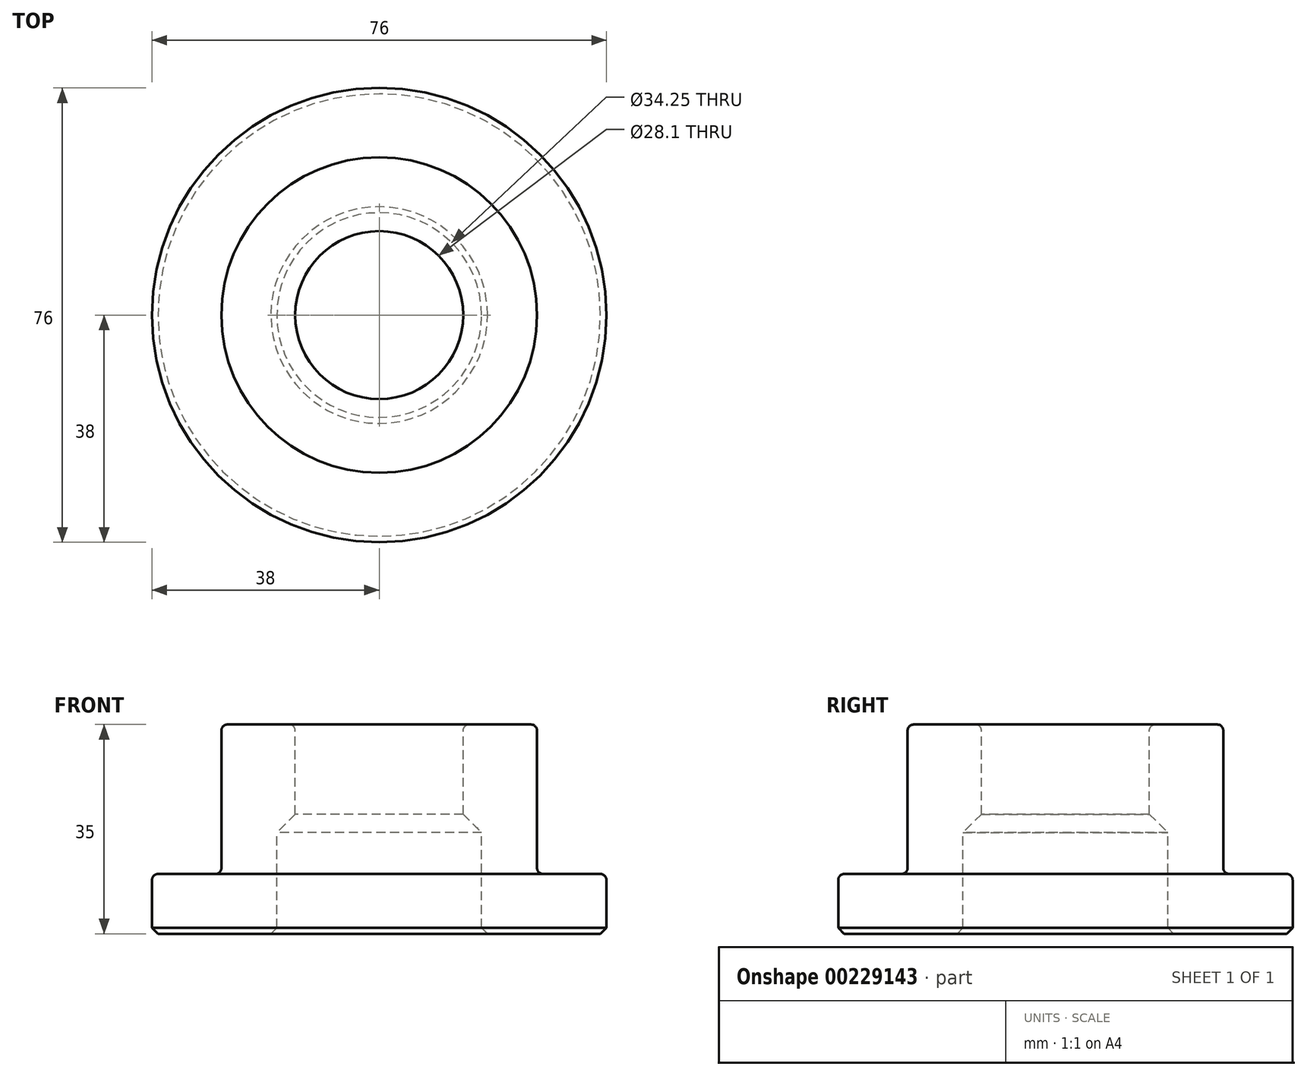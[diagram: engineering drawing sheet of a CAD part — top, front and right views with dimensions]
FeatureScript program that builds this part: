
annotation { "Feature Type Name" : "Feature", "Feature Type Description" : "" }
export const myFeature = defineFeature(function(context is Context, id is Id, definition is map)
    precondition{}
    {
        {
            var Q0;
            Q0=qCreatedBy(makeId("Right.planeOp"),FACE);
            var sketch = newSketch(context, id + "F0", { "sketchPlane" : qUnion([Q0])});
            skLineSegment(sketch, "E0", {"start": v(-38, 0) * mm, "end": v(-38, 10) * mm});
            skLineSegment(sketch, "E1", {"start": v(-38, 10) * mm, "end": v(-26.4, 10) * mm});
            skLineSegment(sketch, "E2", {"start": v(-26.4, 10) * mm, "end": v(-26.4, 35) * mm});
            skLineSegment(sketch, "E3", {"start": v(-26.4, 35) * mm, "end": v(-14.05, 35) * mm});
            skLineSegment(sketch, "E4", {"start": v(-14.05, 35) * mm, "end": v(-14.05, 20) * mm});
            skLineSegment(sketch, "E5", {"start": v(-17.12, 16.93) * mm, "end": v(-17.12, 0) * mm});
            skLineSegment(sketch, "E6", {"start": v(-17.12, 0) * mm, "end": v(-38, 0) * mm});
            skLineSegment(sketch, "E7", {"start": v(0, 68.15) * mm, "end": v(0, -19.01) * mm, "construction": true});
            skLineSegment(sketch, "E8", {"start": v(-14.05, 20) * mm, "end": v(-17.12, 16.93) * mm});
            skPoint(sketch, "E9.orphan", {"position": v(-17.12, 20) * mm});
            skSolve(sketch);
        }
        {
            var Q0;
            Q0 = qSketchRegion(id + "F0", true);
            var Q1;
            Q1=sQuery(id+"F0.wireOp",EDGE,"E7");
            revolve(context, id + "F1", {"entities" : qUnion([Q0]), "axis" : qUnion([Q1]), "revolveType" : RevolveType.FULL});
        }
        {
            var Q0;
            Q0=makeQuery(id+"F1.opRevolve","SWEPT_EDGE",EDGE,{"disambiguationData":[OSD([sQuery(id+"F0.wireOp",EDGE,"E0"),sQuery(id+"F0.wireOp",EDGE,"E6")])]});
            var Q1;
            Q1=makeQuery(id+"F1.opRevolve","SWEPT_EDGE",EDGE,{"disambiguationData":[OSD([sQuery(id+"F0.wireOp",EDGE,"E5"),sQuery(id+"F0.wireOp",EDGE,"E6")])]});
            chamfer(context, id + "F2", {"entities" : qUnion([Q0, Q1]), "width" : 1 * mm, "tangentPropagation" : true});
        }
        {
            var Q0;
            Q0=makeQuery(id+"F1.opRevolve","SWEPT_FACE",FACE,{"disambiguationData":[OSD([sQuery(id+"F0.wireOp",EDGE,"E3")])]});
            var Q1;
            Q1=makeQuery(id+"F1.opRevolve","SWEPT_EDGE",EDGE,{"disambiguationData":[OSD([sQuery(id+"F0.wireOp",EDGE,"E0"),sQuery(id+"F0.wireOp",EDGE,"E1")])]});
            var Q2;
            Q2=makeQuery(id+"F1.opRevolve","SWEPT_EDGE",EDGE,{"disambiguationData":[OSD([sQuery(id+"F0.wireOp",EDGE,"E1"),sQuery(id+"F0.wireOp",EDGE,"E2")])]});
            fillet(context, id + "F3", {"entities" : qUnion([Q0, Q1, Q2]), "radius" : 1 * mm, "tangentPropagation" : true, "allowEdgeOverflow" : false});
        }
    });
